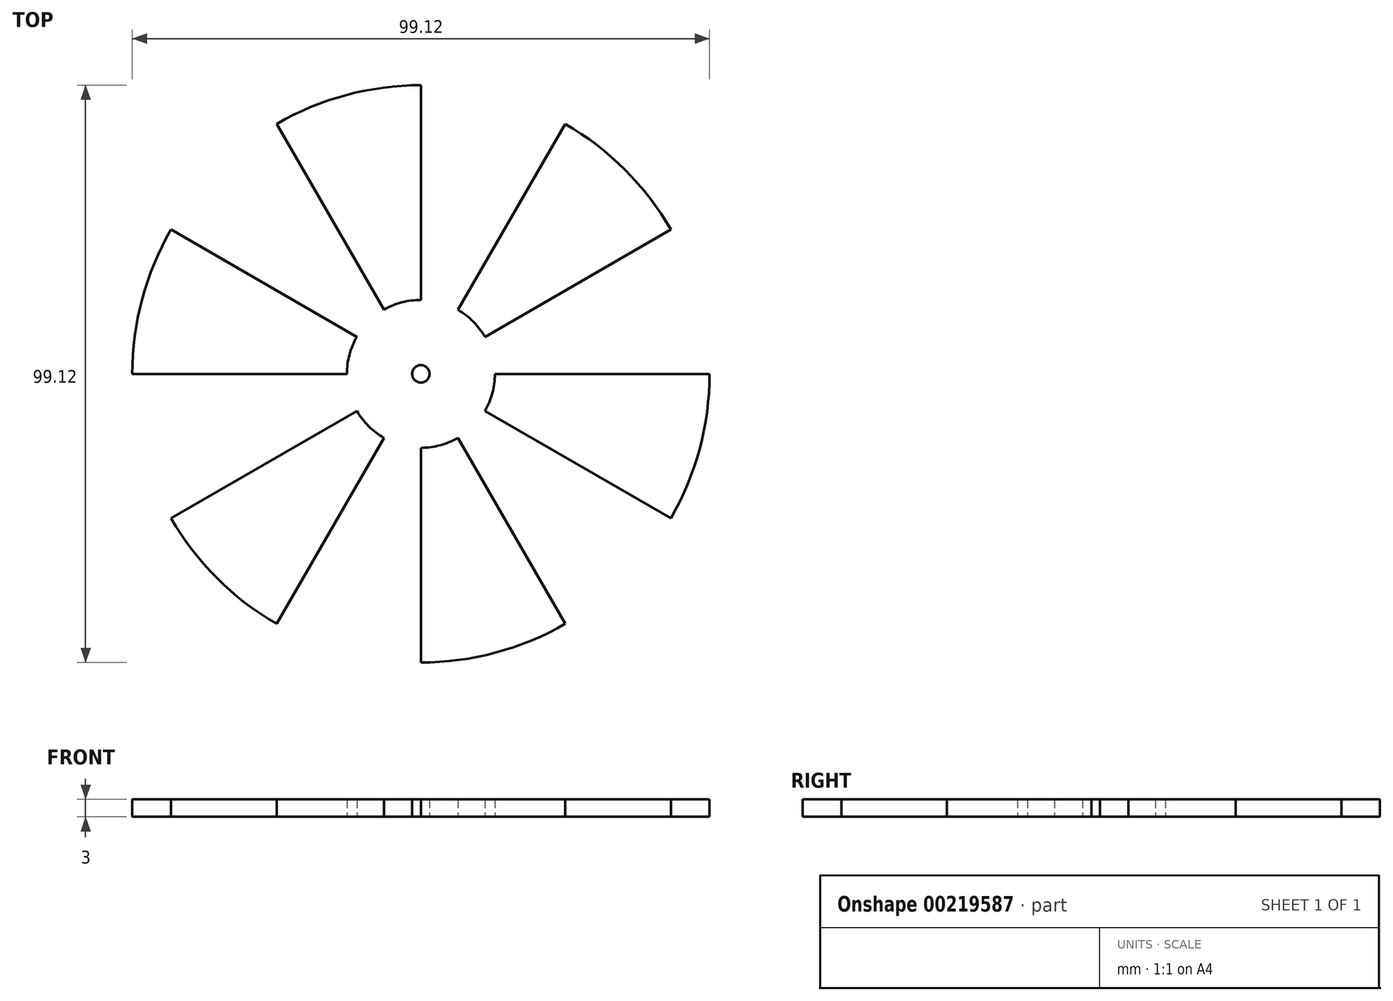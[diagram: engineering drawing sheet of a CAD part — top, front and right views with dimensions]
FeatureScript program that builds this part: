
annotation { "Feature Type Name" : "Feature", "Feature Type Description" : "" }
export const myFeature = defineFeature(function(context is Context, id is Id, definition is map)
    precondition{}
    {
        {
            var Q0;
            Q0=qCreatedBy(makeId("Top.planeOp"),FACE);
            var sketch = newSketch(context, id + "F0", { "sketchPlane" : qUnion([Q0])});
            skLineSegment(sketch, "E0.MirrorCS", {"start": v(-55.54, -350.41) * mm, "end": v(-59.46, -367.58) * mm});
            skArc(sketch, "E1", {"start": v(-55.54, -350.41) * mm, "mid": v(-55.82, -348.75) * mm, "end": v(-57.2, -347.77) * mm});
            skArc(sketch, "E2.13.3", {"start": v(-59.84, -349.43) * mm, "mid": v(-58.86, -348.06) * mm, "end": v(-57.2, -347.78) * mm});
            skLineSegment(sketch, "E2.13.4", {"start": v(-59.84, -349.43) * mm, "end": v(-63.76, -366.6) * mm});
            skArc(sketch, "E3", {"start": v(-32.32, -368.6) * mm, "mid": v(-44.25, -366.6) * mm, "end": v(-56.18, -368.6) * mm});
            skArc(sketch, "E4", {"start": v(-64.24, -366.92) * mm, "mid": v(-63.99, -366.78) * mm, "end": v(-63.76, -366.6) * mm});
            skArc(sketch, "E5.MirrorCS", {"start": v(-59.16, -368.08) * mm, "mid": v(-59.32, -367.84) * mm, "end": v(-59.46, -367.58) * mm});
            skArc(sketch, "E6.1.1", {"start": v(-32.97, -350.41) * mm, "mid": v(-32.68, -348.75) * mm, "end": v(-31.3, -347.77) * mm});
            skArc(sketch, "E6.1.2", {"start": v(-28.67, -349.43) * mm, "mid": v(-29.65, -348.06) * mm, "end": v(-31.3, -347.77) * mm});
            skLineSegment(sketch, "E6.1.3", {"start": v(-28.67, -349.43) * mm, "end": v(-24.75, -366.6) * mm});
            skArc(sketch, "E6.1.6", {"start": v(0.14, -355.74) * mm, "mid": v(-11.48, -359.11) * mm, "end": v(-21.36, -366.1) * mm});
            skLineSegment(sketch, "E6.1.7", {"start": v(-32.97, -350.41) * mm, "end": v(-29.05, -367.58) * mm});
            skArc(sketch, "E6.1.8", {"start": v(-29.34, -368.08) * mm, "mid": v(-29.18, -367.84) * mm, "end": v(-29.05, -367.58) * mm});
            skArc(sketch, "E6.1.9", {"start": v(-24.27, -366.92) * mm, "mid": v(-24.52, -366.78) * mm, "end": v(-24.75, -366.6) * mm});
            skArc(sketch, "E6.2.1", {"start": v(-8.33, -339.64) * mm, "mid": v(-8.8, -338.02) * mm, "end": v(-7.98, -336.54) * mm});
            skArc(sketch, "E6.2.2", {"start": v(-4.89, -336.89) * mm, "mid": v(-6.36, -336.07) * mm, "end": v(-7.98, -336.54) * mm});
            skLineSegment(sketch, "E6.2.3", {"start": v(-4.89, -336.89) * mm, "end": v(6.1, -350.66) * mm});
            skArc(sketch, "E6.2.6", {"start": v(23.81, -330.08) * mm, "mid": v(14.8, -338.15) * mm, "end": v(8.93, -348.73) * mm});
            skLineSegment(sketch, "E6.2.7", {"start": v(-8.33, -339.64) * mm, "end": v(2.65, -353.4) * mm});
            skArc(sketch, "E6.2.8", {"start": v(2.6, -353.99) * mm, "mid": v(2.64, -353.7) * mm, "end": v(2.65, -353.4) * mm});
            skArc(sketch, "E6.2.9", {"start": v(6.67, -350.74) * mm, "mid": v(6.38, -350.72) * mm, "end": v(6.1, -350.66) * mm});
            skArc(sketch, "E6.3.1", {"start": v(9.19, -319.24) * mm, "mid": v(8.06, -317.98) * mm, "end": v(8.16, -316.3) * mm});
            skArc(sketch, "E6.3.2", {"start": v(11.1, -315.27) * mm, "mid": v(9.42, -315.18) * mm, "end": v(8.16, -316.3) * mm});
            skLineSegment(sketch, "E6.3.3", {"start": v(11.1, -315.27) * mm, "end": v(26.97, -322.91) * mm});
            skArc(sketch, "E6.3.6", {"start": v(34, -296.68) * mm, "mid": v(29.39, -307.87) * mm, "end": v(28.69, -319.95) * mm});
            skLineSegment(sketch, "E6.3.7", {"start": v(9.19, -319.24) * mm, "end": v(25.06, -326.88) * mm});
            skArc(sketch, "E6.3.8", {"start": v(25.26, -327.43) * mm, "mid": v(25.18, -327.15) * mm, "end": v(25.06, -326.88) * mm});
            skArc(sketch, "E6.3.9", {"start": v(27.52, -322.73) * mm, "mid": v(27.25, -322.84) * mm, "end": v(26.97, -322.91) * mm});
            skArc(sketch, "E6.4.1", {"start": v(16.12, -293.26) * mm, "mid": v(14.57, -292.62) * mm, "end": v(13.92, -291.06) * mm});
            skArc(sketch, "E6.4.2", {"start": v(16.12, -288.86) * mm, "mid": v(14.57, -289.5) * mm, "end": v(13.92, -291.06) * mm});
            skLineSegment(sketch, "E6.4.3", {"start": v(16.12, -288.86) * mm, "end": v(33.74, -288.86) * mm});
            skArc(sketch, "E6.4.6", {"start": v(28.69, -262.17) * mm, "mid": v(29.39, -274.25) * mm, "end": v(34, -285.44) * mm});
            skLineSegment(sketch, "E6.4.7", {"start": v(16.12, -293.26) * mm, "end": v(33.74, -293.26) * mm});
            skArc(sketch, "E6.4.8", {"start": v(34.16, -293.66) * mm, "mid": v(33.96, -293.45) * mm, "end": v(33.74, -293.26) * mm});
            skArc(sketch, "E6.4.9", {"start": v(34.16, -288.46) * mm, "mid": v(33.96, -288.67) * mm, "end": v(33.74, -288.86) * mm});
            skArc(sketch, "E6.5.1", {"start": v(11.1, -266.85) * mm, "mid": v(9.42, -266.94) * mm, "end": v(8.16, -265.82) * mm});
            skArc(sketch, "E6.5.2", {"start": v(9.19, -262.88) * mm, "mid": v(8.06, -264.14) * mm, "end": v(8.16, -265.82) * mm});
            skLineSegment(sketch, "E6.5.3", {"start": v(9.19, -262.88) * mm, "end": v(25.06, -255.24) * mm});
            skArc(sketch, "E6.5.6", {"start": v(8.93, -233.39) * mm, "mid": v(14.8, -243.97) * mm, "end": v(23.81, -252.04) * mm});
            skLineSegment(sketch, "E6.5.7", {"start": v(11.1, -266.85) * mm, "end": v(26.97, -259.2) * mm});
            skArc(sketch, "E6.5.8", {"start": v(27.52, -259.39) * mm, "mid": v(27.25, -259.28) * mm, "end": v(26.97, -259.2) * mm});
            skArc(sketch, "E6.5.9", {"start": v(25.26, -254.7) * mm, "mid": v(25.18, -254.97) * mm, "end": v(25.06, -255.24) * mm});
            skArc(sketch, "E6.6.1", {"start": v(-4.89, -245.23) * mm, "mid": v(-6.36, -246.05) * mm, "end": v(-7.98, -245.58) * mm});
            skArc(sketch, "E6.6.2", {"start": v(-8.33, -242.48) * mm, "mid": v(-8.8, -244.1) * mm, "end": v(-7.98, -245.58) * mm});
            skLineSegment(sketch, "E6.6.3", {"start": v(-8.33, -242.48) * mm, "end": v(2.65, -228.71) * mm});
            skArc(sketch, "E6.6.6", {"start": v(-21.36, -216.02) * mm, "mid": v(-11.48, -223) * mm, "end": v(0.14, -226.38) * mm});
            skLineSegment(sketch, "E6.6.7", {"start": v(-4.89, -245.23) * mm, "end": v(6.1, -231.46) * mm});
            skArc(sketch, "E6.6.8", {"start": v(6.67, -231.38) * mm, "mid": v(6.38, -231.4) * mm, "end": v(6.1, -231.46) * mm});
            skArc(sketch, "E6.6.9", {"start": v(2.6, -228.13) * mm, "mid": v(2.64, -228.42) * mm, "end": v(2.65, -228.71) * mm});
            skArc(sketch, "E6.7.1", {"start": v(-28.67, -232.69) * mm, "mid": v(-29.65, -234.06) * mm, "end": v(-31.3, -234.34) * mm});
            skArc(sketch, "E6.7.2", {"start": v(-32.97, -231.7) * mm, "mid": v(-32.68, -233.37) * mm, "end": v(-31.3, -234.35) * mm});
            skLineSegment(sketch, "E6.7.3", {"start": v(-32.97, -231.7) * mm, "end": v(-29.05, -214.54) * mm});
            skArc(sketch, "E6.7.6", {"start": v(-56.18, -213.52) * mm, "mid": v(-44.25, -215.53) * mm, "end": v(-32.32, -213.52) * mm});
            skLineSegment(sketch, "E6.7.7", {"start": v(-28.67, -232.69) * mm, "end": v(-24.75, -215.52) * mm});
            skArc(sketch, "E6.7.8", {"start": v(-24.27, -215.2) * mm, "mid": v(-24.52, -215.34) * mm, "end": v(-24.75, -215.52) * mm});
            skArc(sketch, "E6.7.9", {"start": v(-29.34, -214.04) * mm, "mid": v(-29.18, -214.28) * mm, "end": v(-29.05, -214.54) * mm});
            skArc(sketch, "E6.8.1", {"start": v(-55.54, -231.7) * mm, "mid": v(-55.82, -233.37) * mm, "end": v(-57.2, -234.35) * mm});
            skArc(sketch, "E6.8.2", {"start": v(-59.84, -232.69) * mm, "mid": v(-58.86, -234.06) * mm, "end": v(-57.2, -234.35) * mm});
            skLineSegment(sketch, "E6.8.3", {"start": v(-59.84, -232.69) * mm, "end": v(-63.76, -215.52) * mm});
            skArc(sketch, "E6.8.6", {"start": v(-88.65, -226.38) * mm, "mid": v(-77.03, -223) * mm, "end": v(-67.15, -216.02) * mm});
            skLineSegment(sketch, "E6.8.7", {"start": v(-55.54, -231.7) * mm, "end": v(-59.46, -214.54) * mm});
            skArc(sketch, "E6.8.8", {"start": v(-59.16, -214.04) * mm, "mid": v(-59.32, -214.28) * mm, "end": v(-59.46, -214.54) * mm});
            skArc(sketch, "E6.8.9", {"start": v(-64.24, -215.2) * mm, "mid": v(-63.99, -215.34) * mm, "end": v(-63.76, -215.52) * mm});
            skArc(sketch, "E6.9.1", {"start": v(-80.17, -242.48) * mm, "mid": v(-79.7, -244.1) * mm, "end": v(-80.52, -245.58) * mm});
            skArc(sketch, "E6.9.2", {"start": v(-83.62, -245.23) * mm, "mid": v(-82.14, -246.05) * mm, "end": v(-80.52, -245.58) * mm});
            skLineSegment(sketch, "E6.9.3", {"start": v(-83.62, -245.23) * mm, "end": v(-94.6, -231.46) * mm});
            skArc(sketch, "E6.9.6", {"start": v(-112.32, -252.04) * mm, "mid": v(-103.3, -243.97) * mm, "end": v(-97.44, -233.39) * mm});
            skLineSegment(sketch, "E6.9.7", {"start": v(-80.17, -242.48) * mm, "end": v(-91.15, -228.71) * mm});
            skArc(sketch, "E6.9.8", {"start": v(-91.1, -228.13) * mm, "mid": v(-91.15, -228.42) * mm, "end": v(-91.15, -228.71) * mm});
            skArc(sketch, "E6.9.9", {"start": v(-95.18, -231.38) * mm, "mid": v(-94.89, -231.4) * mm, "end": v(-94.6, -231.46) * mm});
            skArc(sketch, "E6.10.1", {"start": v(-97.7, -262.88) * mm, "mid": v(-96.57, -264.14) * mm, "end": v(-96.67, -265.82) * mm});
            skArc(sketch, "E6.10.2", {"start": v(-99.6, -266.85) * mm, "mid": v(-97.92, -266.94) * mm, "end": v(-96.66, -265.82) * mm});
            skLineSegment(sketch, "E6.10.3", {"start": v(-99.6, -266.85) * mm, "end": v(-115.47, -259.2) * mm});
            skArc(sketch, "E6.10.6", {"start": v(-122.5, -285.44) * mm, "mid": v(-117.9, -274.25) * mm, "end": v(-117.2, -262.17) * mm});
            skLineSegment(sketch, "E6.10.7", {"start": v(-97.7, -262.88) * mm, "end": v(-113.56, -255.24) * mm});
            skArc(sketch, "E6.10.8", {"start": v(-113.77, -254.7) * mm, "mid": v(-113.68, -254.97) * mm, "end": v(-113.56, -255.24) * mm});
            skArc(sketch, "E6.10.9", {"start": v(-116.03, -259.39) * mm, "mid": v(-115.76, -259.28) * mm, "end": v(-115.47, -259.2) * mm});
            skArc(sketch, "E6.11.1", {"start": v(-104.63, -288.86) * mm, "mid": v(-103.07, -289.5) * mm, "end": v(-102.43, -291.06) * mm});
            skArc(sketch, "E6.11.2", {"start": v(-104.63, -293.26) * mm, "mid": v(-103.07, -292.62) * mm, "end": v(-102.43, -291.06) * mm});
            skLineSegment(sketch, "E6.11.3", {"start": v(-104.63, -293.26) * mm, "end": v(-122.24, -293.26) * mm});
            skArc(sketch, "E6.11.6", {"start": v(-117.2, -319.95) * mm, "mid": v(-117.9, -307.87) * mm, "end": v(-122.5, -296.68) * mm});
            skLineSegment(sketch, "E6.11.7", {"start": v(-104.63, -288.86) * mm, "end": v(-122.24, -288.86) * mm});
            skArc(sketch, "E6.11.8", {"start": v(-122.66, -288.46) * mm, "mid": v(-122.46, -288.67) * mm, "end": v(-122.24, -288.86) * mm});
            skArc(sketch, "E6.11.9", {"start": v(-122.66, -293.66) * mm, "mid": v(-122.46, -293.45) * mm, "end": v(-122.24, -293.26) * mm});
            skArc(sketch, "E6.12.1", {"start": v(-99.6, -315.27) * mm, "mid": v(-97.92, -315.18) * mm, "end": v(-96.66, -316.3) * mm});
            skArc(sketch, "E6.12.2", {"start": v(-97.7, -319.24) * mm, "mid": v(-96.57, -317.98) * mm, "end": v(-96.67, -316.3) * mm});
            skLineSegment(sketch, "E6.12.3", {"start": v(-97.7, -319.24) * mm, "end": v(-113.56, -326.88) * mm});
            skArc(sketch, "E6.12.6", {"start": v(-97.44, -348.73) * mm, "mid": v(-103.3, -338.15) * mm, "end": v(-112.32, -330.08) * mm});
            skLineSegment(sketch, "E6.12.7", {"start": v(-99.6, -315.27) * mm, "end": v(-115.47, -322.91) * mm});
            skArc(sketch, "E6.12.8", {"start": v(-116.03, -322.73) * mm, "mid": v(-115.76, -322.84) * mm, "end": v(-115.47, -322.91) * mm});
            skArc(sketch, "E6.12.9", {"start": v(-113.77, -327.43) * mm, "mid": v(-113.68, -327.15) * mm, "end": v(-113.56, -326.88) * mm});
            skArc(sketch, "E6.13.1", {"start": v(-83.62, -336.89) * mm, "mid": v(-82.14, -336.07) * mm, "end": v(-80.52, -336.54) * mm});
            skArc(sketch, "E6.13.2", {"start": v(-80.17, -339.64) * mm, "mid": v(-79.7, -338.02) * mm, "end": v(-80.52, -336.54) * mm});
            skLineSegment(sketch, "E6.13.3", {"start": v(-80.17, -339.64) * mm, "end": v(-91.15, -353.4) * mm});
            skPoint(sketch, "E6.13.4", {"position": v(-86.04, -347) * mm});
            skArc(sketch, "E6.13.6", {"start": v(-67.15, -366.1) * mm, "mid": v(-77.02, -359.11) * mm, "end": v(-88.65, -355.74) * mm});
            skLineSegment(sketch, "E6.13.7", {"start": v(-83.62, -336.89) * mm, "end": v(-94.6, -350.66) * mm});
            skArc(sketch, "E6.13.8", {"start": v(-95.18, -350.74) * mm, "mid": v(-94.89, -350.72) * mm, "end": v(-94.6, -350.66) * mm});
            skArc(sketch, "E6.13.9", {"start": v(-91.1, -353.99) * mm, "mid": v(-91.15, -353.7) * mm, "end": v(-91.15, -353.4) * mm});
            skArc(sketch, "E7", {"start": v(34, -296.68) * mm, "mid": v(34.1, -295.17) * mm, "end": v(34.16, -293.66) * mm});
            skPoint(sketch, "E8.orphan", {"position": v(34.43, -294.08) * mm});
            skPoint(sketch, "E9.orphan", {"position": v(34.32, -296.18) * mm});
            skArc(sketch, "E10.trimOffspring", {"start": v(34.16, -288.46) * mm, "mid": v(34.1, -286.95) * mm, "end": v(34, -285.44) * mm});
            skArc(sketch, "E11.trimOffspring", {"start": v(28.69, -262.17) * mm, "mid": v(28.12, -260.77) * mm, "end": v(27.52, -259.39) * mm});
            skPoint(sketch, "E12.orphan", {"position": v(34.43, -288.04) * mm});
            skArc(sketch, "E13.trimOffspring", {"start": v(25.26, -254.7) * mm, "mid": v(24.55, -253.36) * mm, "end": v(23.81, -252.04) * mm});
            skPoint(sketch, "E14.orphan", {"position": v(27.95, -259.64) * mm});
            skPoint(sketch, "E15.orphan", {"position": v(28.76, -261.58) * mm});
            skArc(sketch, "E16.trimOffspring", {"start": v(8.93, -233.39) * mm, "mid": v(7.81, -232.37) * mm, "end": v(6.67, -231.38) * mm});
            skPoint(sketch, "E17.orphan", {"position": v(25.33, -254.2) * mm});
            skArc(sketch, "E18.trimOffspring", {"start": v(2.6, -228.13) * mm, "mid": v(1.38, -227.24) * mm, "end": v(0.14, -226.38) * mm});
            skPoint(sketch, "E19.orphan", {"position": v(7.17, -231.43) * mm});
            skPoint(sketch, "E20.orphan", {"position": v(8.74, -232.82) * mm});
            skPoint(sketch, "E21.orphan", {"position": v(2.44, -227.66) * mm});
            skArc(sketch, "E22.trimOffspring", {"start": v(-21.36, -216.02) * mm, "mid": v(-22.8, -215.6) * mm, "end": v(-24.27, -215.2) * mm});
            skArc(sketch, "E23.trimOffspring", {"start": v(-56.18, -213.52) * mm, "mid": v(-57.68, -213.76) * mm, "end": v(-59.16, -214.04) * mm});
            skPoint(sketch, "E24.orphan", {"position": v(-29.69, -213.68) * mm});
            skArc(sketch, "E25.trimOffspring", {"start": v(-29.34, -214.04) * mm, "mid": v(-30.83, -213.76) * mm, "end": v(-32.32, -213.52) * mm});
            skPoint(sketch, "E26.orphan", {"position": v(-21.78, -215.6) * mm});
            skPoint(sketch, "E27.orphan", {"position": v(-23.8, -215.02) * mm});
            skArc(sketch, "E28.trimOffspring", {"start": v(-88.65, -226.38) * mm, "mid": v(-89.88, -227.24) * mm, "end": v(-91.1, -228.13) * mm});
            skPoint(sketch, "E29.orphan", {"position": v(-64.7, -215.02) * mm});
            skArc(sketch, "E30.trimOffspring", {"start": v(-64.24, -215.2) * mm, "mid": v(-65.7, -215.6) * mm, "end": v(-67.15, -216.02) * mm});
            skPoint(sketch, "E31.orphan", {"position": v(-56.75, -213.32) * mm});
            skPoint(sketch, "E32.orphan", {"position": v(-58.82, -213.68) * mm});
            skPoint(sketch, "E33.orphan", {"position": v(-89.24, -226.44) * mm});
            skPoint(sketch, "E34.orphan", {"position": v(-90.95, -227.66) * mm});
            skArc(sketch, "E35.trimOffspring", {"start": v(-95.18, -231.38) * mm, "mid": v(-96.32, -232.37) * mm, "end": v(-97.44, -233.39) * mm});
            skPoint(sketch, "E36.orphan", {"position": v(-95.67, -231.43) * mm});
            skArc(sketch, "E37.trimOffspring", {"start": v(-112.32, -252.04) * mm, "mid": v(-113.05, -253.36) * mm, "end": v(-113.77, -254.7) * mm});
            skArc(sketch, "E38.trimOffspring", {"start": v(-122.5, -285.44) * mm, "mid": v(-122.6, -286.95) * mm, "end": v(-122.66, -288.46) * mm});
            skArc(sketch, "E39.trimOffspring", {"start": v(-116.03, -259.39) * mm, "mid": v(-116.62, -260.77) * mm, "end": v(-117.2, -262.17) * mm});
            skPoint(sketch, "E40.orphan", {"position": v(-112.82, -252.36) * mm});
            skPoint(sketch, "E41.orphan", {"position": v(-113.83, -254.2) * mm});
            skPoint(sketch, "E42.orphan", {"position": v(-122.83, -285.94) * mm});
            skPoint(sketch, "E43.orphan", {"position": v(-122.93, -288.04) * mm});
            skArc(sketch, "E44.trimOffspring", {"start": v(-122.66, -293.66) * mm, "mid": v(-122.6, -295.17) * mm, "end": v(-122.5, -296.68) * mm});
            skPoint(sketch, "E45.orphan", {"position": v(-122.93, -294.08) * mm});
            skArc(sketch, "E46.trimOffspring", {"start": v(-117.2, -319.95) * mm, "mid": v(-116.62, -321.35) * mm, "end": v(-116.03, -322.73) * mm});
            skPoint(sketch, "E47.orphan", {"position": v(-117.26, -320.54) * mm});
            skPoint(sketch, "E48.orphan", {"position": v(-116.45, -322.48) * mm});
            skArc(sketch, "E49.trimOffspring", {"start": v(-113.77, -327.43) * mm, "mid": v(-113.05, -328.76) * mm, "end": v(-112.32, -330.08) * mm});
            skPoint(sketch, "E50.orphan", {"position": v(-113.83, -327.92) * mm});
            skArc(sketch, "E51.trimOffspring", {"start": v(-97.44, -348.73) * mm, "mid": v(-96.32, -349.75) * mm, "end": v(-95.18, -350.74) * mm});
            skPoint(sketch, "E52.orphan", {"position": v(-95.67, -350.7) * mm});
            skPoint(sketch, "E53.orphan", {"position": v(-97.24, -349.3) * mm});
            skArc(sketch, "E54.trimOffspring", {"start": v(-91.1, -353.99) * mm, "mid": v(-89.88, -354.88) * mm, "end": v(-88.65, -355.74) * mm});
            skPoint(sketch, "E55.orphan", {"position": v(-90.95, -354.46) * mm});
            skArc(sketch, "E56.trimOffspring", {"start": v(-67.15, -366.1) * mm, "mid": v(-65.7, -366.53) * mm, "end": v(-64.24, -366.92) * mm});
            skPoint(sketch, "E57.orphan", {"position": v(-64.7, -367.1) * mm});
            skPoint(sketch, "E58.orphan", {"position": v(-66.72, -366.52) * mm});
            skArc(sketch, "E59.trimOffspring", {"start": v(-59.16, -368.08) * mm, "mid": v(-57.68, -368.36) * mm, "end": v(-56.18, -368.6) * mm});
            skPoint(sketch, "E60.orphan", {"position": v(-58.82, -368.44) * mm});
            skArc(sketch, "E61.trimOffspring", {"start": v(-32.32, -368.6) * mm, "mid": v(-30.83, -368.36) * mm, "end": v(-29.34, -368.08) * mm});
            skPoint(sketch, "E62.orphan", {"position": v(-31.76, -368.8) * mm});
            skPoint(sketch, "E63.orphan", {"position": v(-29.69, -368.44) * mm});
            skArc(sketch, "E64.trimOffspring", {"start": v(-24.27, -366.92) * mm, "mid": v(-22.8, -366.53) * mm, "end": v(-21.36, -366.1) * mm});
            skPoint(sketch, "E65.orphan", {"position": v(-23.8, -367.1) * mm});
            skArc(sketch, "E66.trimOffspring", {"start": v(0.14, -355.74) * mm, "mid": v(1.38, -354.88) * mm, "end": v(2.6, -353.99) * mm});
            skPoint(sketch, "E67.orphan", {"position": v(0.74, -355.68) * mm});
            skPoint(sketch, "E68.orphan", {"position": v(2.44, -354.46) * mm});
            skArc(sketch, "E69.trimOffspring", {"start": v(6.67, -350.74) * mm, "mid": v(7.81, -349.75) * mm, "end": v(8.93, -348.73) * mm});
            skPoint(sketch, "E70.orphan", {"position": v(7.17, -350.7) * mm});
            skArc(sketch, "E71.trimOffspring", {"start": v(23.81, -330.08) * mm, "mid": v(24.55, -328.76) * mm, "end": v(25.26, -327.43) * mm});
            skArc(sketch, "E72.trimOffspring", {"start": v(27.52, -322.73) * mm, "mid": v(28.12, -321.35) * mm, "end": v(28.69, -319.95) * mm});
            skPoint(sketch, "E73.orphan", {"position": v(25.33, -327.92) * mm});
            skPoint(sketch, "E74.orphan", {"position": v(24.32, -329.76) * mm});
            skPoint(sketch, "E75.orphan", {"position": v(27.95, -322.48) * mm});
            skCircle(sketch, "E76", {"center": v(-44.25, -291.06) * mm, "radius": 1.5 * mm});
            skArc(sketch, "E77", {"start": v(-55.25, -284.7) * mm, "mid": v(-56.52, -287.77) * mm, "end": v(-56.95, -291.06) * mm});
            skArc(sketch, "E78", {"start": v(-87.17, -266.28) * mm, "mid": v(-92.12, -278.23) * mm, "end": v(-93.81, -291.06) * mm});
            skLineSegment(sketch, "E79", {"start": v(-44.25, -291.06) * mm, "end": v(-44.25, -289.56) * mm});
            skLineSegment(sketch, "E80", {"start": v(-44.25, -291.06) * mm, "end": v(-43.5, -289.76) * mm});
            skLineSegment(sketch, "E81", {"start": v(-44.25, -291.06) * mm, "end": v(-42.95, -290.3) * mm});
            skLineSegment(sketch, "E82", {"start": v(-44.25, -291.06) * mm, "end": v(-42.75, -291.06) * mm});
            skLineSegment(sketch, "E83.MirrorCS", {"start": v(-44.25, -291.06) * mm, "end": v(-42.95, -291.8) * mm});
            skLineSegment(sketch, "E84.MirrorCS", {"start": v(-44.25, -291.06) * mm, "end": v(-43.5, -292.36) * mm});
            skLineSegment(sketch, "E85.MirrorCS", {"start": v(-44.25, -291.06) * mm, "end": v(-44.25, -292.56) * mm});
            skLineSegment(sketch, "E86.MirrorCS", {"start": v(-44.25, -291.06) * mm, "end": v(-45, -292.36) * mm});
            skLineSegment(sketch, "E87.MirrorCS", {"start": v(-44.25, -291.06) * mm, "end": v(-45.55, -291.8) * mm});
            skLineSegment(sketch, "E88.MirrorCS", {"start": v(-44.25, -291.06) * mm, "end": v(-45.75, -291.06) * mm});
            skLineSegment(sketch, "E89.MirrorCS", {"start": v(-44.25, -291.06) * mm, "end": v(-45.55, -290.3) * mm});
            skLineSegment(sketch, "E90.MirrorCS", {"start": v(-44.25, -291.06) * mm, "end": v(-45, -289.76) * mm});
            skLineSegment(sketch, "E91.trimOffspring", {"start": v(-50.6, -280.06) * mm, "end": v(-69.03, -248.14) * mm});
            skLineSegment(sketch, "E92.trimOffspring", {"start": v(-55.25, -284.7) * mm, "end": v(-87.17, -266.28) * mm});
            skLineSegment(sketch, "E93.trimOffspring", {"start": v(-56.95, -291.06) * mm, "end": v(-93.81, -291.06) * mm});
            skLineSegment(sketch, "E94.trimOffspring", {"start": v(-55.25, -297.4) * mm, "end": v(-87.17, -315.84) * mm});
            skLineSegment(sketch, "E95.trimOffspring", {"start": v(-50.6, -302.06) * mm, "end": v(-69.03, -333.98) * mm});
            skLineSegment(sketch, "E96.trimOffspring", {"start": v(-44.25, -303.76) * mm, "end": v(-44.25, -340.62) * mm});
            skLineSegment(sketch, "E97.trimOffspring", {"start": v(-37.9, -302.06) * mm, "end": v(-19.47, -333.98) * mm});
            skLineSegment(sketch, "E98.trimOffspring", {"start": v(-33.25, -297.4) * mm, "end": v(-1.33, -315.84) * mm});
            skLineSegment(sketch, "E99.trimOffspring", {"start": v(-31.55, -291.06) * mm, "end": v(5.3, -291.06) * mm});
            skLineSegment(sketch, "E100.trimOffspring", {"start": v(-33.25, -284.7) * mm, "end": v(-1.33, -266.28) * mm});
            skLineSegment(sketch, "E101.trimOffspring", {"start": v(-37.9, -280.06) * mm, "end": v(-19.47, -248.14) * mm});
            skLineSegment(sketch, "E102.trimOffspring", {"start": v(-44.25, -278.36) * mm, "end": v(-44.25, -241.5) * mm});
            skPoint(sketch, "E103.trimOffspring.end.orphan", {"position": v(-44.25, -241.5) * mm});
            skArc(sketch, "E104.trimOffspring", {"start": v(-55.25, -297.4) * mm, "mid": v(-53.23, -300.04) * mm, "end": v(-50.6, -302.06) * mm});
            skArc(sketch, "E105.trimOffspring", {"start": v(-87.17, -315.84) * mm, "mid": v(-79.3, -326.1) * mm, "end": v(-69.03, -333.98) * mm});
            skArc(sketch, "E106.trimOffspring", {"start": v(-44.25, -303.76) * mm, "mid": v(-40.97, -303.33) * mm, "end": v(-37.9, -302.06) * mm});
            skArc(sketch, "E107.trimOffspring", {"start": v(-44.25, -340.62) * mm, "mid": v(-31.43, -338.93) * mm, "end": v(-19.47, -333.98) * mm});
            skArc(sketch, "E108.trimOffspring", {"start": v(-33.25, -297.4) * mm, "mid": v(-31.99, -294.35) * mm, "end": v(-31.55, -291.06) * mm});
            skArc(sketch, "E109.trimOffspring", {"start": v(-1.33, -315.84) * mm, "mid": v(3.62, -303.89) * mm, "end": v(5.3, -291.06) * mm});
            skArc(sketch, "E110.trimOffspring", {"start": v(-1.33, -266.28) * mm, "mid": v(-9.2, -256.02) * mm, "end": v(-19.47, -248.14) * mm});
            skArc(sketch, "E111.trimOffspring", {"start": v(-33.25, -284.7) * mm, "mid": v(-35.27, -282.08) * mm, "end": v(-37.9, -280.06) * mm});
            skArc(sketch, "E112.trimOffspring", {"start": v(-44.25, -241.5) * mm, "mid": v(-57.08, -243.19) * mm, "end": v(-69.03, -248.14) * mm});
            skArc(sketch, "E113.trimOffspring", {"start": v(-44.25, -278.36) * mm, "mid": v(-47.54, -278.8) * mm, "end": v(-50.6, -280.06) * mm});
            skSolve(sketch);
        }
        {
            var Q0;
            Q0 = qSketchRegion(id + "F0", true);
            extrude(context, id + "F1", {"entities" : qUnion([Q0]), "depth" : 3 * mm});
        }
    });
